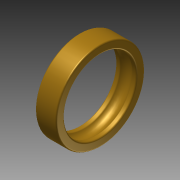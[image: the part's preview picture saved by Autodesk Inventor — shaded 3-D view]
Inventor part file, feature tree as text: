
AUTODESK INVENTOR PART (.ipt)
format: ipt  version: 2011 SP2 (Build 150309200, 309)  size: 156,672 bytes
history: native  units: mm
features: revolve x1, fillet x1, sketch x1
ambient origin geometry x8: Origin, YZ Plane, XZ Plane, XY Plane, X Axis, Y Axis, Z Axis, Center Point
bodies: Solid1 (feature_tree)
feature tree (3):
  revolve  "Revolution1"  [1 undecoded]
  fillet  "Fillet1"  Radius=53.0mm
  sketch  "Sketch1"  dims[d0=31.0mm d1=65.0mm d2=53.0mm d3=12.0mm d4=8.0mm d5=90.0deg d6=2.0mm]
note: 1 required parameter value undecoded (feature->parameter linkage not recoverable at this tier; creation-order binding heuristic only, values carry confidence <= 0.55)
